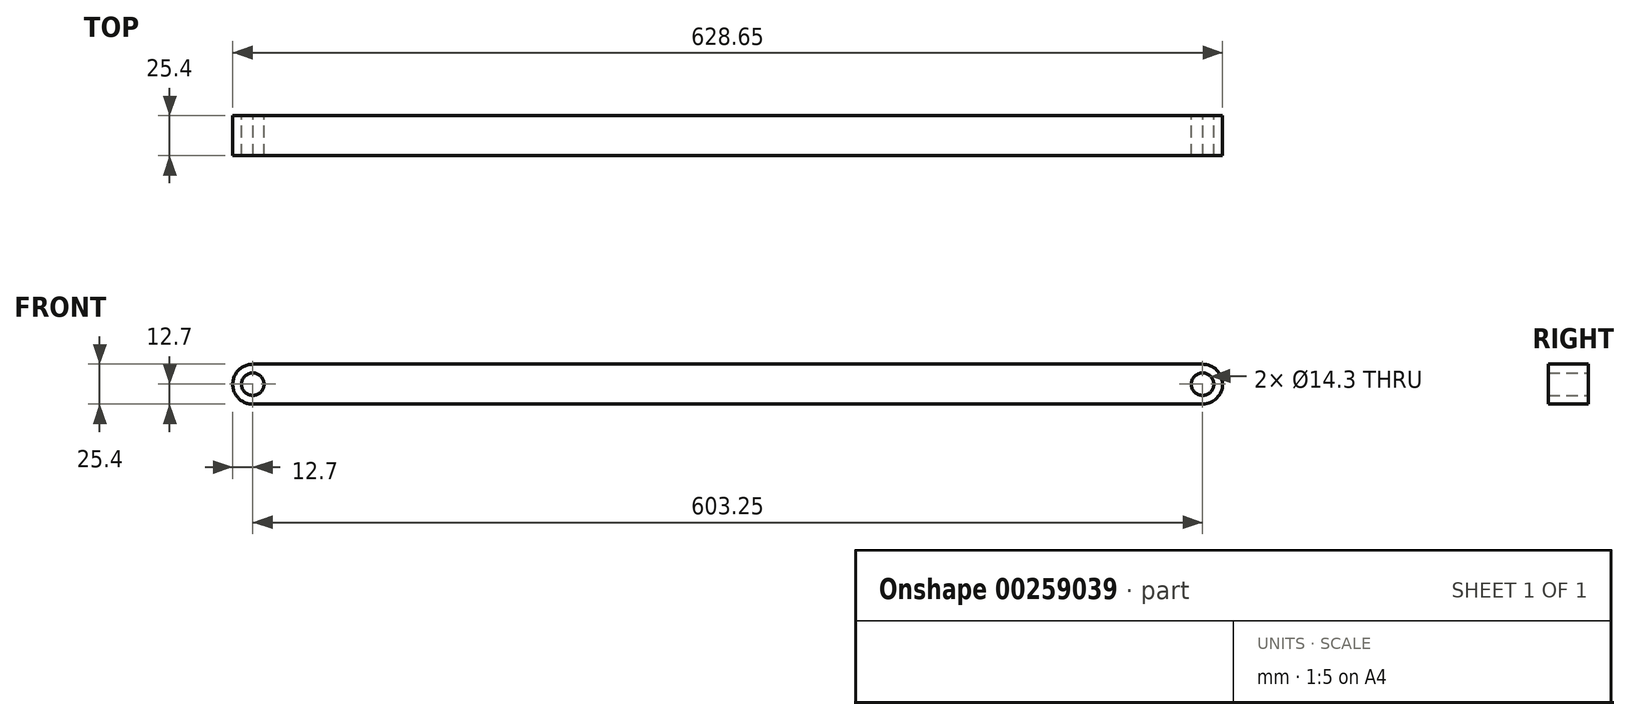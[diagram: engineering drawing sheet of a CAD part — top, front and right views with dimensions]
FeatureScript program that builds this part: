
annotation { "Feature Type Name" : "Feature", "Feature Type Description" : "" }
export const myFeature = defineFeature(function(context is Context, id is Id, definition is map)
    precondition{}
    {
        {
            var Q0;
            Q0=qCreatedBy(makeId("Front.planeOp"),FACE);
            var sketch = newSketch(context, id + "F0", { "sketchPlane" : qUnion([Q0])});
            skCircle(sketch, "E0", {"center": v(0, 0) * mm, "radius": 12.7 * mm});
            skCircle(sketch, "E1", {"center": v(0, 0) * mm, "radius": 7.15 * mm});
            skCircle(sketch, "E2", {"center": v(603.25, 0) * mm, "radius": 12.7 * mm});
            skCircle(sketch, "E3", {"center": v(603.25, 0) * mm, "radius": 7.15 * mm});
            skLineSegment(sketch, "E4", {"start": v(0, 12.7) * mm, "end": v(603.25, 12.7) * mm});
            skLineSegment(sketch, "E5", {"start": v(603.5, -12.7) * mm, "end": v(0, -12.7) * mm});
            skSolve(sketch);
        }
        {
            var Q0;
            {var subQ0=sQuery(id+"F0.wireOp",EDGE,"E4");Q0=makeQuery(id+"F0.imprint","IMPRINT",FACE,{"disambiguationData":[TD([[makeQuery(id+"F0.imprint","IMPRINT",EDGE,{"derivedFrom":subQ0}),-1.0]])]});}
            var Q1;
            Q1=makeQuery(id+"F0.imprint","IMPRINT",FACE,{"disambiguationData":[TD([[makeQuery(id+"F0.imprint","IMPRINT",EDGE,{"derivedFrom":sQuery(id+"F0.wireOp",EDGE,"E1")}),-1.0]])]});
            var Q2;
            Q2=makeQuery(id+"F0.imprint","IMPRINT",FACE,{"disambiguationData":[TD([[makeQuery(id+"F0.imprint","IMPRINT",EDGE,{"derivedFrom":sQuery(id+"F0.wireOp",EDGE,"E3")}),-1.0]])]});
            extrude(context, id + "F1", {"entities" : qUnion([Q0, Q1, Q2]), "depth" : 25.4 * mm});
        }
    });
